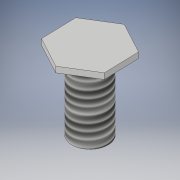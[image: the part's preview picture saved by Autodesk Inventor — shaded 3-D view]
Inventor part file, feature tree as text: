
AUTODESK INVENTOR PART (.ipt)
format: ipt  version: 2017 (Build 210142000, 142)  size: 111,616 bytes
history: native  units: in
note: dims shown in document units (in); Inventor stores cm internally (conversion verified against a paired STEP export)
features: extrude x2, thread x2, sketch x2
ambient origin geometry x8: Origin, YZ Plane, XZ Plane, XY Plane, X Axis, Y Axis, Z Axis, Center Point
bodies: Solid1 (feature_tree)
feature tree (6):
  extrude  "Extrusion1"  Depth=0.25in
  thread  "Thread1"  [1 undecoded]
  extrude  "Extrusion3"  Depth=0.02in TaperAngle=0.0deg
  thread  "Thread3"  [1 undecoded]
  sketch  "Sketch1"  dims[d0=0.5in d1=0.125in d2=0.25in d3=0.0in]
  sketch  "Sketch3"  dims[d7=1.0in d8=0.0in d11=0.02in d12=0.0in d13=1.0in d14=0.0in]
note: 2 required parameter values undecoded (feature->parameter linkage not recoverable at this tier; creation-order binding heuristic only, values carry confidence <= 0.55)
